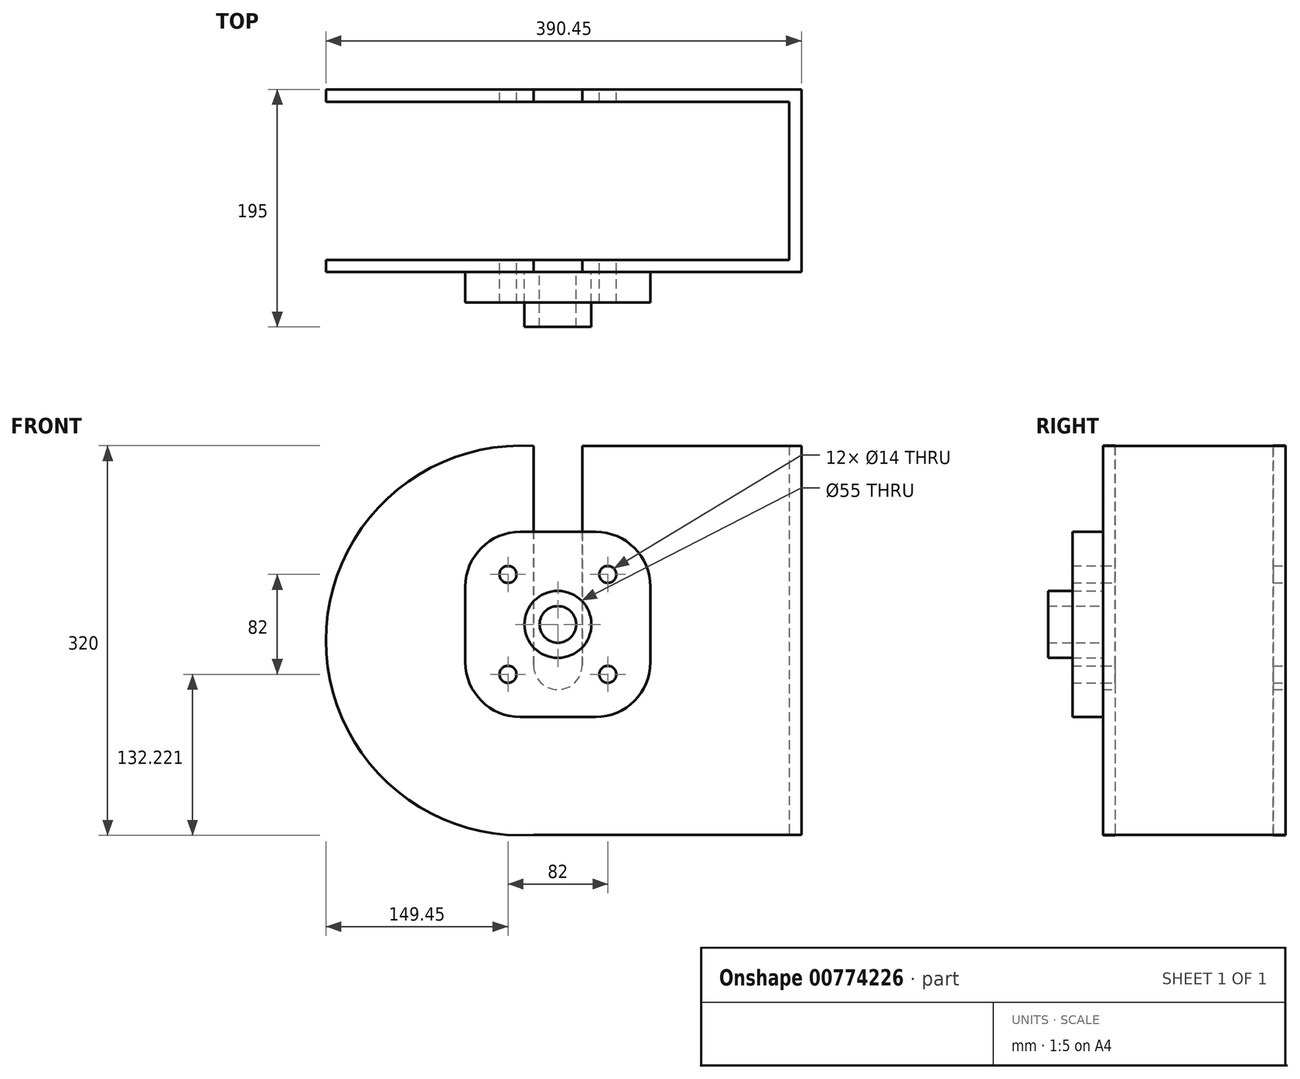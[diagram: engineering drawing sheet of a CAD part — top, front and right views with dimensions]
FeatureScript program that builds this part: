
annotation { "Feature Type Name" : "Feature", "Feature Type Description" : "" }
export const myFeature = defineFeature(function(context is Context, id is Id, definition is map)
    precondition{}
    {
        {
            var Q0;
            Q0=qCreatedBy(makeId("Front.planeOp"),FACE);
            var sketch = newSketch(context, id + "F0", { "sketchPlane" : qUnion([Q0])});
            skLineSegment(sketch, "E0", {"start": v(20, 319.32) * mm, "end": v(20, 139.32) * mm});
            skLineSegment(sketch, "E1", {"start": v(-20, 139.32) * mm, "end": v(-20, 319.32) * mm});
            skArc(sketch, "E2", {"start": v(-20, 139.32) * mm, "mid": v(0, 119.32) * mm, "end": v(20, 139.32) * mm});
            skLineSegment(sketch, "E3", {"start": v(-229.36, 172.88) * mm, "end": v(278.04, 172.88) * mm, "construction": true});
            skCircle(sketch, "E4", {"center": v(-41, 213.88) * mm, "radius": 7 * mm});
            skCircle(sketch, "E5", {"center": v(-41, 131.88) * mm, "radius": 7 * mm});
            skLineSegment(sketch, "E6", {"start": v(0, 0) * mm, "end": v(0, 354.33) * mm, "construction": true});
            skCircle(sketch, "E7.MirrorC", {"center": v(41, 213.88) * mm, "radius": 7 * mm});
            skCircle(sketch, "E8.MirrorC", {"center": v(41, 131.88) * mm, "radius": 7 * mm});
            skLineSegment(sketch, "E9", {"start": v(-20, 319.32) * mm, "end": v(-20, -13.4) * mm, "construction": true});
            skLineSegment(sketch, "E10", {"start": v(20, 319.32) * mm, "end": v(200, 319.32) * mm});
            skLineSegment(sketch, "E11", {"start": v(200, 319.32) * mm, "end": v(200, 0) * mm});
            skArc(sketch, "E12", {"start": v(-20, 319.32) * mm, "mid": v(-190.45, 159.66) * mm, "end": v(-20, 0) * mm});
            skLineSegment(sketch, "E13", {"start": v(-20, 0) * mm, "end": v(200, 0) * mm});
            skSolve(sketch);
        }
        {
            var Q0;
            Q0 = qSketchRegion(id + "F0", true);
            extrude(context, id + "F1", {"entities" : qUnion([Q0]), "depth" : 150 * mm, "offsetDistance" : 25 * mm});
        }
        {
            var Q0;
            Q0=makeQuery(id+"F1.opExtrude","SWEPT_FACE",FACE,{"disambiguationData":[OSD([sQuery(id+"F0.wireOp",EDGE,"E13")])]});
            var sketch = newSketch(context, id + "F2", { "sketchPlane" : qUnion([Q0])});
            skLineSegment(sketch, "E14", {"start": v(-200, 10) * mm, "end": v(190, 10) * mm});
            skLineSegment(sketch, "E15", {"start": v(190, 10) * mm, "end": v(190, 140) * mm});
            skLineSegment(sketch, "E16", {"start": v(190, 140) * mm, "end": v(-200, 140) * mm});
            skLineSegment(sketch, "E17", {"start": v(-200, 140) * mm, "end": v(-200, 10) * mm});
            skSolve(sketch);
        }
        {
            var Q0;
            Q0 = qSketchRegion(id + "F2", true);
            extrude(context, id + "F3", {"entities" : qUnion([Q0]), "operationType" : NewBodyOperationType.REMOVE, "endBound" : BoundingType.SYMMETRIC, "oppositeDirection" : true, "depth" : 10000 * mm, "offsetDistance" : 25 * mm});
        }
        {
            var Q0;
            Q0=makeQuery(id+"F1.opExtrude","CAP_FACE",FACE,{"disambiguationData":[OSD([sQuery(id+"F0.wireOp",EDGE,"E0"),sQuery(id+"F0.wireOp",EDGE,"E1"),sQuery(id+"F0.wireOp",EDGE,"E2"),sQuery(id+"F0.wireOp",EDGE,"E4"),sQuery(id+"F0.wireOp",EDGE,"E5"),sQuery(id+"F0.wireOp",EDGE,"E7.MirrorC"),sQuery(id+"F0.wireOp",EDGE,"E8.MirrorC"),sQuery(id+"F0.wireOp",EDGE,"E10"),sQuery(id+"F0.wireOp",EDGE,"E11"),sQuery(id+"F0.wireOp",EDGE,"E12"),sQuery(id+"F0.wireOp",EDGE,"E13")])],"isStart":false});
            var sketch = newSketch(context, id + "F4", { "sketchPlane" : qUnion([Q0])});
            skLineSegment(sketch, "E18.bottom", {"start": v(-31, 96.88) * mm, "end": v(31, 96.88) * mm});
            skLineSegment(sketch, "E18.top", {"start": v(-31, 248.88) * mm, "end": v(31, 248.88) * mm});
            skLineSegment(sketch, "E18.left", {"start": v(-76, 141.88) * mm, "end": v(-76, 203.88) * mm});
            skLineSegment(sketch, "E18.right", {"start": v(76, 141.88) * mm, "end": v(76, 203.88) * mm});
            skPoint(sketch, "E19.visualSharp", {"position": v(-76, 96.88) * mm});
            skArc(sketch, "E19.filletArc", {"start": v(-76, 141.88) * mm, "mid": v(-62.82, 110.06) * mm, "end": v(-31, 96.88) * mm});
            skPoint(sketch, "E20.visualSharp", {"position": v(76, 96.88) * mm});
            skArc(sketch, "E20.filletArc", {"start": v(31, 96.88) * mm, "mid": v(62.82, 110.06) * mm, "end": v(76, 141.88) * mm});
            skPoint(sketch, "E21.visualSharp", {"position": v(76, 248.88) * mm});
            skArc(sketch, "E21.filletArc", {"start": v(76, 203.88) * mm, "mid": v(62.82, 235.7) * mm, "end": v(31, 248.88) * mm});
            skPoint(sketch, "E22.visualSharp", {"position": v(-76, 248.88) * mm});
            skArc(sketch, "E22.filletArc", {"start": v(-31, 248.88) * mm, "mid": v(-62.82, 235.7) * mm, "end": v(-76, 203.88) * mm});
            skCircle(sketch, "E23", {"center": v(-41, 131.88) * mm, "radius": 7 * mm});
            skCircle(sketch, "E24", {"center": v(41, 131.88) * mm, "radius": 7 * mm});
            skCircle(sketch, "E25", {"center": v(-41, 213.88) * mm, "radius": 7 * mm});
            skCircle(sketch, "E26", {"center": v(41, 213.88) * mm, "radius": 7 * mm});
            skCircle(sketch, "E27", {"center": v(0, 172.88) * mm, "radius": 27.5 * mm});
            skPoint(sketch, "E27.centerSnap0", {"position": v(-76, 172.88) * mm});
            skSolve(sketch);
        }
        {
            var Q0;
            Q0 = qSketchRegion(id + "F4", true);
            extrude(context, id + "F5", {"entities" : qUnion([Q0]), "depth" : 25 * mm, "offsetDistance" : 25 * mm});
        }
        {
            var Q0;
            Q0=makeQuery(id+"F5.opExtrude","CAP_FACE",FACE,{"disambiguationData":[OSD([sQuery(id+"F4.wireOp",EDGE,"E18.bottom"),sQuery(id+"F4.wireOp",EDGE,"E18.top"),sQuery(id+"F4.wireOp",EDGE,"E18.left"),sQuery(id+"F4.wireOp",EDGE,"E18.right"),sQuery(id+"F4.wireOp",EDGE,"E19.filletArc"),sQuery(id+"F4.wireOp",EDGE,"E20.filletArc"),sQuery(id+"F4.wireOp",EDGE,"E21.filletArc"),sQuery(id+"F4.wireOp",EDGE,"E22.filletArc"),sQuery(id+"F4.wireOp",EDGE,"E23"),sQuery(id+"F4.wireOp",EDGE,"E24"),sQuery(id+"F4.wireOp",EDGE,"E25"),sQuery(id+"F4.wireOp",EDGE,"E26"),sQuery(id+"F4.wireOp",EDGE,"E27")])],"isStart":true});
            var sketch = newSketch(context, id + "F6", { "sketchPlane" : qUnion([Q0])});
            skCircle(sketch, "E28", {"center": v(0, 172.88) * mm, "radius": 27.5 * mm});
            skCircle(sketch, "E29", {"center": v(0, 172.88) * mm, "radius": 15 * mm});
            skSolve(sketch);
        }
        {
            var Q0;
            Q0 = qSketchRegion(id + "F6", true);
            extrude(context, id + "F7", {"entities" : qUnion([Q0]), "oppositeDirection" : true, "depth" : 45 * mm, "offsetDistance" : 25 * mm});
        }
    });
